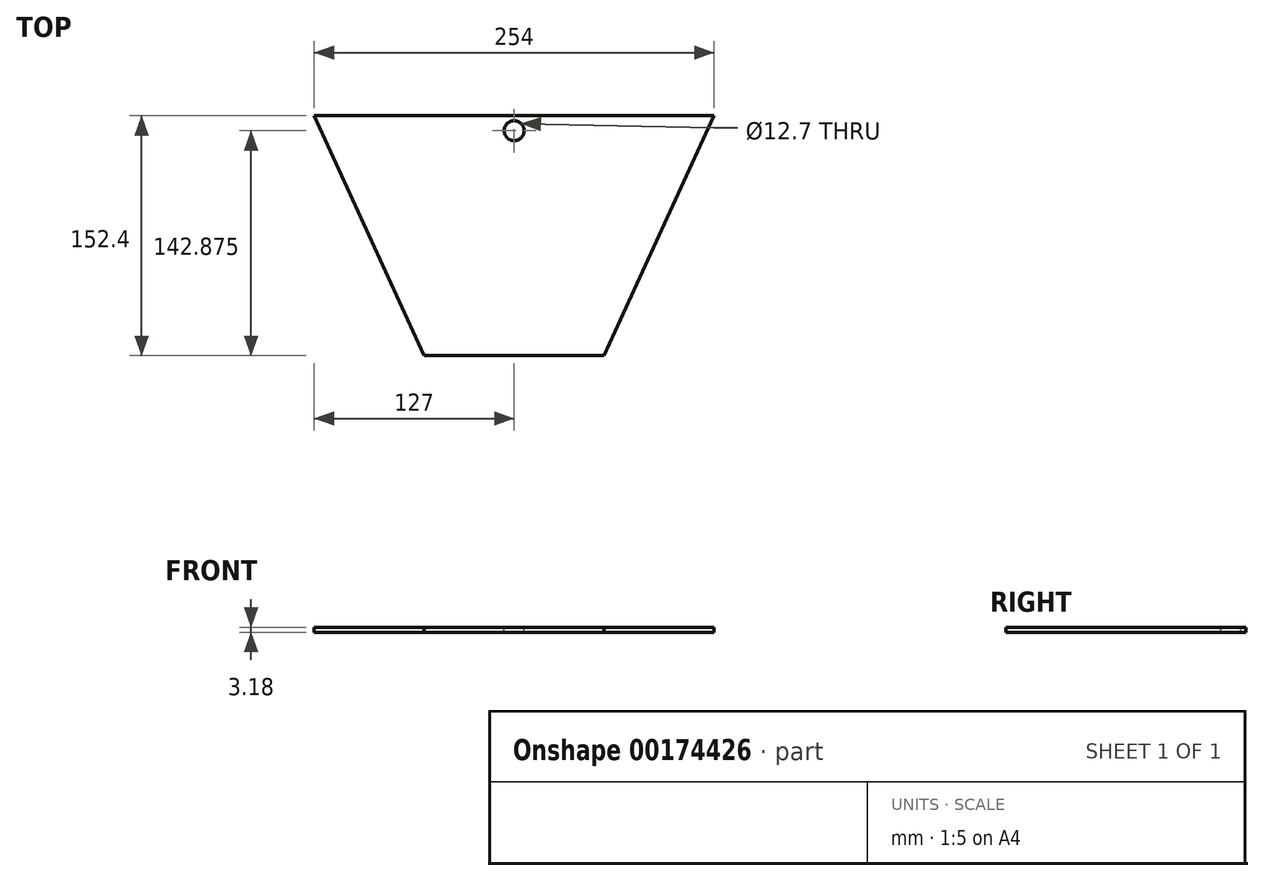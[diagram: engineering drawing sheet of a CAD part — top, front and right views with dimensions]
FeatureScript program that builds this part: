
annotation { "Feature Type Name" : "Feature", "Feature Type Description" : "" }
export const myFeature = defineFeature(function(context is Context, id is Id, definition is map)
    precondition{}
    {
        {
            var Q0;
            Q0=qCreatedBy(makeId("Top.planeOp"),FACE);
            var sketch = newSketch(context, id + "F0", { "sketchPlane" : qUnion([Q0])});
            skLineSegment(sketch, "E0.bottom", {"start": v(127, 76.2) * mm, "end": v(-127, 76.2) * mm});
            skLineSegment(sketch, "E0.top", {"start": v(57.15, -76.2) * mm, "end": v(-57.15, -76.2) * mm});
            skPoint(sketch, "E0.middle", {"position": v(0, 0) * mm});
            skLineSegment(sketch, "E1", {"start": v(-127, 76.2) * mm, "end": v(-57.15, -76.2) * mm});
            skLineSegment(sketch, "E2", {"start": v(127, 76.2) * mm, "end": v(57.15, -76.2) * mm});
            skPoint(sketch, "E3.orphan", {"position": v(-127, -76.2) * mm});
            skPoint(sketch, "E4.orphan", {"position": v(127, -76.2) * mm});
            skSolve(sketch);
        }
        {
            var Q0;
            Q0 = qSketchRegion(id + "F0", true);
            extrude(context, id + "F1", {"entities" : qUnion([Q0]), "depth" : 3.17 * mm});
        }
        {
            var Q0;
            Q0=makeQuery(id+"F1.opExtrude","CAP_FACE",FACE,{"disambiguationData":[OSD([sQuery(id+"F0.wireOp",EDGE,"E0.bottom"),sQuery(id+"F0.wireOp",EDGE,"E0.top"),sQuery(id+"F0.wireOp",EDGE,"E1"),sQuery(id+"F0.wireOp",EDGE,"E2")])],"isStart":false});
            var sketch = newSketch(context, id + "F2", { "sketchPlane" : qUnion([Q0])});
            skCircle(sketch, "E5", {"center": v(0, 66.67) * mm, "radius": 6.35 * mm});
            skSolve(sketch);
        }
        {
            var Q0;
            Q0 = qSketchRegion(id + "F2", true);
            extrude(context, id + "F3", {"entities" : qUnion([Q0]), "operationType" : NewBodyOperationType.REMOVE, "oppositeDirection" : true, "depth" : 25.4 * mm});
        }
    });
